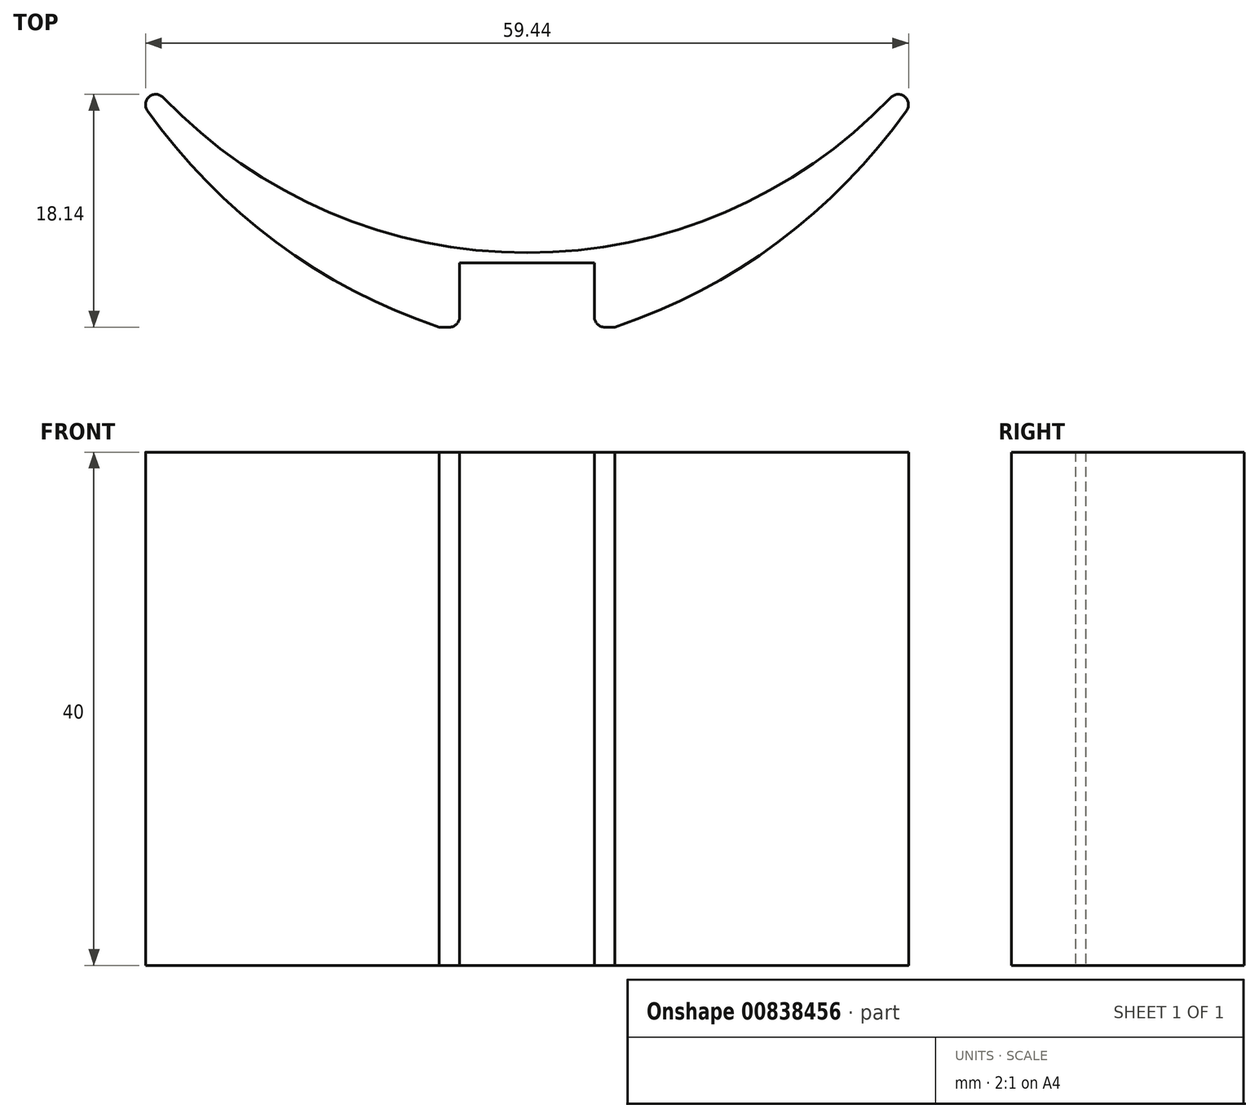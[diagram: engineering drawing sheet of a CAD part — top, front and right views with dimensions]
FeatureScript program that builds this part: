
annotation { "Feature Type Name" : "Feature", "Feature Type Description" : "" }
export const myFeature = defineFeature(function(context is Context, id is Id, definition is map)
    precondition{}
    {
        {
            var Q0;
            Q0=qCreatedBy(makeId("Top.planeOp"),FACE);
            var sketch = newSketch(context, id + "F0", { "sketchPlane" : qUnion([Q0])});
            skArc(sketch, "E0", {"start": v(-35.25, 0) * mm, "mid": v(0, -22) * mm, "end": v(35.25, 0) * mm});
            skPoint(sketch, "E1", {"position": v(0, -22) * mm});
            skLineSegment(sketch, "E2", {"start": v(-5.25, -27.8) * mm, "end": v(-5.25, -22.8) * mm});
            skLineSegment(sketch, "E3", {"start": v(-5.25, -22.8) * mm, "end": v(5.25, -22.8) * mm});
            skLineSegment(sketch, "E4", {"start": v(5.25, -22.8) * mm, "end": v(5.25, -27.8) * mm});
            skPoint(sketch, "E5", {"position": v(0, -22.8) * mm});
            skLineSegment(sketch, "E6", {"start": v(-5.25, -27.8) * mm, "end": v(-6.85, -27.8) * mm});
            skArc(sketch, "E7", {"start": v(-35.25, 0) * mm, "mid": v(-24.25, -17.16) * mm, "end": v(-6.85, -27.8) * mm});
            skLineSegment(sketch, "E8.MirrorCS", {"start": v(5.25, -27.8) * mm, "end": v(6.85, -27.8) * mm});
            skArc(sketch, "E9.MirrorCS", {"start": v(35.25, 0) * mm, "mid": v(24.25, -17.16) * mm, "end": v(6.85, -27.8) * mm});
            skSolve(sketch);
        }
        {
            var Q0;
            Q0 = qSketchRegion(id + "F0", true);
            extrude(context, id + "F1", {"entities" : qUnion([Q0]), "depth" : 40 * mm, "offsetDistance" : 25 * mm});
        }
        {
            var Q0;
            Q0=makeQuery(id+"F1.opExtrude","SWEPT_EDGE",EDGE,{"disambiguationData":[OSD([sQuery(id+"F0.wireOp",EDGE,"E0"),sQuery(id+"F0.wireOp",EDGE,"E7")])]});
            var Q1;
            Q1=makeQuery(id+"F1.opExtrude","SWEPT_EDGE",EDGE,{"disambiguationData":[OSD([sQuery(id+"F0.wireOp",EDGE,"E0"),sQuery(id+"F0.wireOp",EDGE,"E9.MirrorCS")])]});
            var Q2;
            Q2=makeQuery(id+"F1.opExtrude","SWEPT_EDGE",EDGE,{"disambiguationData":[OSD([sQuery(id+"F0.wireOp",EDGE,"E2"),sQuery(id+"F0.wireOp",EDGE,"E6")])]});
            var Q3;
            Q3=makeQuery(id+"F1.opExtrude","SWEPT_EDGE",EDGE,{"disambiguationData":[OSD([sQuery(id+"F0.wireOp",EDGE,"E4"),sQuery(id+"F0.wireOp",EDGE,"E8.MirrorCS")])]});
            fillet(context, id + "F2", {"entities" : qUnion([Q0, Q1, Q2, Q3]), "tangentPropagation" : true, "radius" : 0.8 * mm, "defaultsChanged" : false, "vertexSettings" : [], "allowEdgeOverflow" : false});
        }
    });
